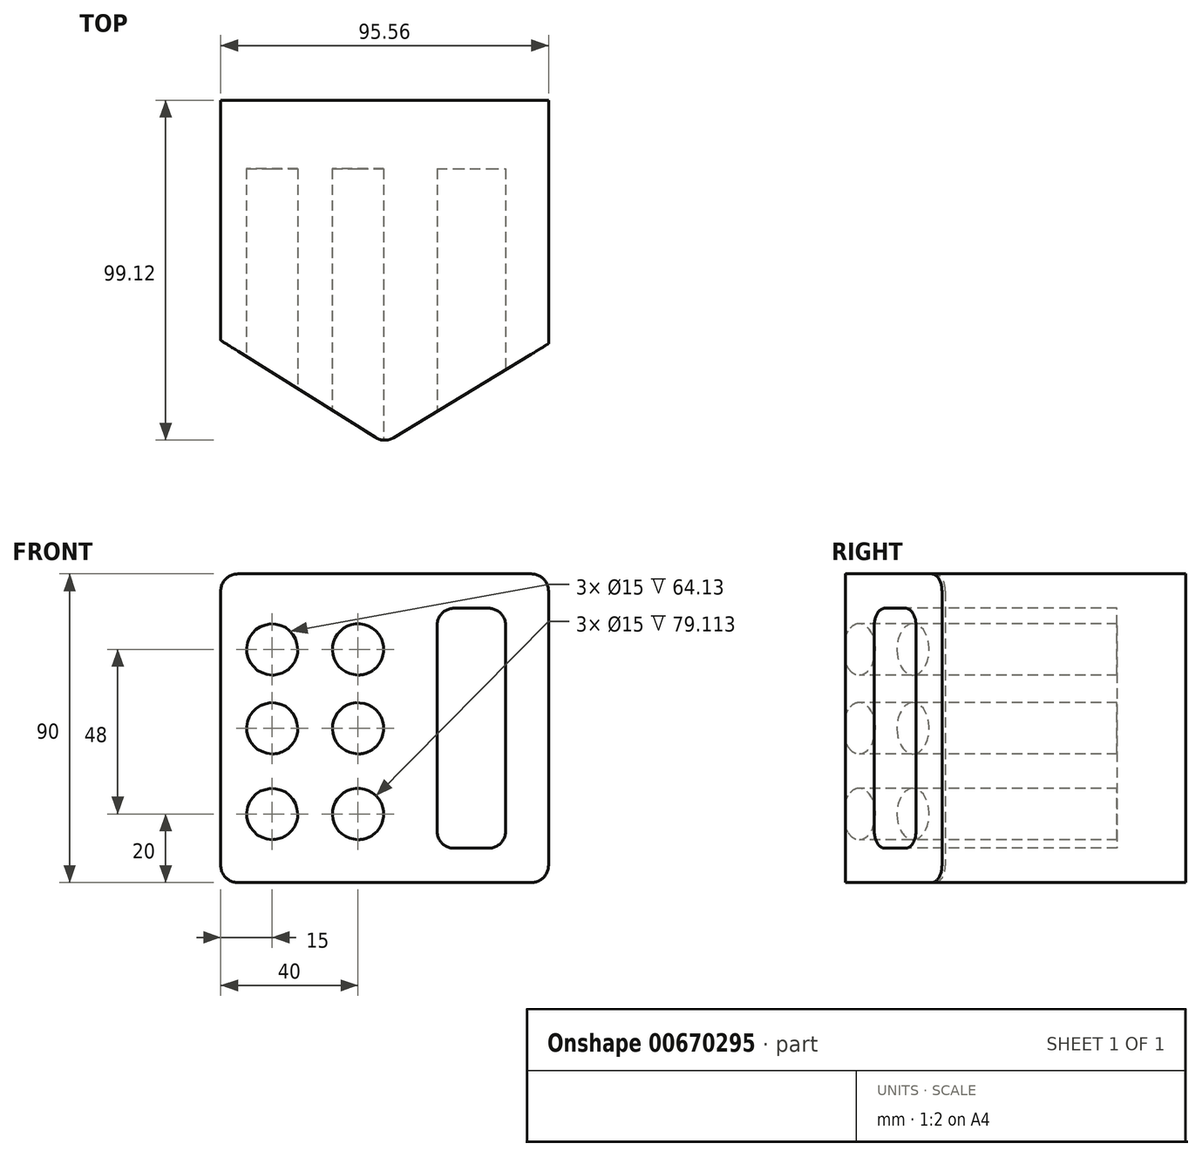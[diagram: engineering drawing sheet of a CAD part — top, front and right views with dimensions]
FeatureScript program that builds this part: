
annotation { "Feature Type Name" : "Feature", "Feature Type Description" : "" }
export const myFeature = defineFeature(function(context is Context, id is Id, definition is map)
    precondition{}
    {
        {
            var Q0;
            Q0=qCreatedBy(makeId("Front.planeOp"),FACE);
            var sketch = newSketch(context, id + "F0", { "sketchPlane" : qUnion([Q0])});
            skLineSegment(sketch, "E0.bottom", {"start": v(0, 0) * mm, "end": v(95.56, 0) * mm});
            skLineSegment(sketch, "E0.top", {"start": v(0, 90) * mm, "end": v(95.56, 90) * mm});
            skLineSegment(sketch, "E0.left", {"start": v(0, 0) * mm, "end": v(0, 90) * mm});
            skLineSegment(sketch, "E0.right", {"start": v(95.56, 0) * mm, "end": v(95.56, 90) * mm});
            skSolve(sketch);
        }
        {
            var Q0;
            Q0 = qSketchRegion(id + "F0", true);
            extrude(context, id + "F1", {"entities" : qUnion([Q0]), "depth" : 100 * mm, "offsetDistance" : 25 * mm});
        }
        {
            var Q0;
            Q0=makeQuery(id+"F1.opExtrude","SWEPT_EDGE",EDGE,{"disambiguationData":[OSD([sQuery(id+"F0.wireOp",EDGE,"E0.top"),sQuery(id+"F0.wireOp",EDGE,"E0.right")])]});
            var Q1;
            Q1=makeQuery(id+"F1.opExtrude","SWEPT_EDGE",EDGE,{"disambiguationData":[OSD([sQuery(id+"F0.wireOp",EDGE,"E0.bottom"),sQuery(id+"F0.wireOp",EDGE,"E0.right")])]});
            var Q2;
            Q2=makeQuery(id+"F1.opExtrude","SWEPT_EDGE",EDGE,{"disambiguationData":[OSD([sQuery(id+"F0.wireOp",EDGE,"E0.bottom"),sQuery(id+"F0.wireOp",EDGE,"E0.left")])]});
            var Q3;
            Q3=makeQuery(id+"F1.opExtrude","SWEPT_EDGE",EDGE,{"disambiguationData":[OSD([sQuery(id+"F0.wireOp",EDGE,"E0.top"),sQuery(id+"F0.wireOp",EDGE,"E0.left")])]});
            fillet(context, id + "F2", {"entities" : qUnion([Q0, Q1, Q2, Q3]), "radius" : 5 * mm, "tangentPropagation" : true, "allowEdgeOverflow" : false});
        }
        {
            var Q0;
            Q0=makeQuery(id+"F1.opExtrude","CAP_FACE",FACE,{"disambiguationData":[OSD([sQuery(id+"F0.wireOp",EDGE,"E0.bottom"),sQuery(id+"F0.wireOp",EDGE,"E0.top"),sQuery(id+"F0.wireOp",EDGE,"E0.left"),sQuery(id+"F0.wireOp",EDGE,"E0.right")])],"isStart":false});
            var sketch = newSketch(context, id + "F3", { "sketchPlane" : qUnion([Q0])});
            skLineSegment(sketch, "E1.bottom", {"start": v(63.06, 80) * mm, "end": v(83.06, 80) * mm});
            skLineSegment(sketch, "E1.top", {"start": v(63.06, 10) * mm, "end": v(83.06, 10) * mm});
            skLineSegment(sketch, "E1.left", {"start": v(63.06, 80) * mm, "end": v(63.06, 10) * mm});
            skLineSegment(sketch, "E1.right", {"start": v(83.06, 80) * mm, "end": v(83.06, 10) * mm});
            skCircle(sketch, "E2", {"center": v(15, 45) * mm, "radius": 7.5 * mm});
            skCircle(sketch, "E3.0.1.0", {"center": v(15, 68) * mm, "radius": 7.5 * mm});
            skCircle(sketch, "E3.1.0.0", {"center": v(40, 45) * mm, "radius": 7.5 * mm});
            skCircle(sketch, "E3.1.1.0", {"center": v(40, 68) * mm, "radius": 7.5 * mm});
            skLineSegment(sketch, "E3.direction1", {"start": v(15, 45) * mm, "end": v(40, 45) * mm, "construction": true});
            skLineSegment(sketch, "E3.direction2", {"start": v(15, 45) * mm, "end": v(15, 68) * mm, "construction": true});
            skCircle(sketch, "E4.0.1.0", {"center": v(15, 20) * mm, "radius": 7.5 * mm});
            skCircle(sketch, "E4.0.1.1", {"center": v(40, 20) * mm, "radius": 7.5 * mm});
            skLineSegment(sketch, "E4.direction2", {"start": v(15, 45) * mm, "end": v(15, 20) * mm, "construction": true});
            skSolve(sketch);
        }
        {
            var Q0;
            Q0 = qSketchRegion(id + "F3", true);
            extrude(context, id + "F4", {"entities" : qUnion([Q0]), "operationType" : NewBodyOperationType.REMOVE, "oppositeDirection" : true, "depth" : 80 * mm, "offsetDistance" : 25 * mm});
        }
        {
            var Q0;
            Q0=makeQuery(id+"F4.boolean.opBoolean","COPY",EDGE,{"derivedFrom":makeQuery(id+"F4.opExtrude","SWEPT_EDGE",EDGE,{"disambiguationData":[OSD([sQuery(id+"F3.wireOp",EDGE,"E1.bottom"),sQuery(id+"F3.wireOp",EDGE,"E1.left")])]})});
            var Q1;
            Q1=makeQuery(id+"F4.boolean.opBoolean","COPY",EDGE,{"derivedFrom":makeQuery(id+"F4.opExtrude","SWEPT_EDGE",EDGE,{"disambiguationData":[OSD([sQuery(id+"F3.wireOp",EDGE,"E1.bottom"),sQuery(id+"F3.wireOp",EDGE,"E1.right")])]})});
            var Q2;
            Q2=makeQuery(id+"F4.boolean.opBoolean","COPY",EDGE,{"derivedFrom":makeQuery(id+"F4.opExtrude","SWEPT_EDGE",EDGE,{"disambiguationData":[OSD([sQuery(id+"F3.wireOp",EDGE,"E1.top"),sQuery(id+"F3.wireOp",EDGE,"E1.right")])]})});
            var Q3;
            Q3=makeQuery(id+"F4.boolean.opBoolean","COPY",EDGE,{"derivedFrom":makeQuery(id+"F4.opExtrude","SWEPT_EDGE",EDGE,{"disambiguationData":[OSD([sQuery(id+"F3.wireOp",EDGE,"E1.top"),sQuery(id+"F3.wireOp",EDGE,"E1.left")])]})});
            fillet(context, id + "F5", {"entities" : qUnion([Q0, Q1, Q2, Q3]), "radius" : 5 * mm, "tangentPropagation" : true, "allowEdgeOverflow" : false});
        }
        {
            var Q0;
            Q0=makeQuery(id+"F1.opExtrude","SWEPT_FACE",FACE,{"disambiguationData":[OSD([sQuery(id+"F0.wireOp",EDGE,"E0.bottom")])]});
            var sketch = newSketch(context, id + "F6", { "sketchPlane" : qUnion([Q0])});
            skPoint(sketch, "E5", {"position": v(47.78, 100) * mm});
            skPoint(sketch, "E6", {"position": v(0, 70) * mm});
            skLineSegment(sketch, "E7", {"start": v(0, 70) * mm, "end": v(47.78, 100) * mm});
            skLineSegment(sketch, "E8", {"start": v(47.78, 100) * mm, "end": v(97.2, 70) * mm});
            skLineSegment(sketch, "E9", {"start": v(97.2, 70) * mm, "end": v(97.2, 124.7) * mm});
            skLineSegment(sketch, "E10", {"start": v(97.2, 124.7) * mm, "end": v(0, 124.7) * mm});
            skLineSegment(sketch, "E11", {"start": v(0, 124.7) * mm, "end": v(0, 70) * mm});
            skSolve(sketch);
        }
        {
            var Q0;
            Q0 = qSketchRegion(id + "F6", true);
            extrude(context, id + "F7", {"entities" : qUnion([Q0]), "operationType" : NewBodyOperationType.REMOVE, "oppositeDirection" : true, "depth" : 90 * mm, "offsetDistance" : 25 * mm});
        }
        {
            var Q0;
            Q0=makeQuery(id+"F7.boolean.opBoolean","COPY",EDGE,{"derivedFrom":makeQuery(id+"F7.opExtrude","SWEPT_EDGE",EDGE,{"disambiguationData":[OSD([sQuery(id+"F0.wireOp",EDGE,"E0.bottom"),sQuery(id+"F6.wireOp",EDGE,"E7"),sQuery(id+"F6.wireOp",EDGE,"E8")])]})});
            fillet(context, id + "F8", {"entities" : qUnion([Q0]), "radius" : 5 * mm, "tangentPropagation" : true, "allowEdgeOverflow" : false});
        }
    });
